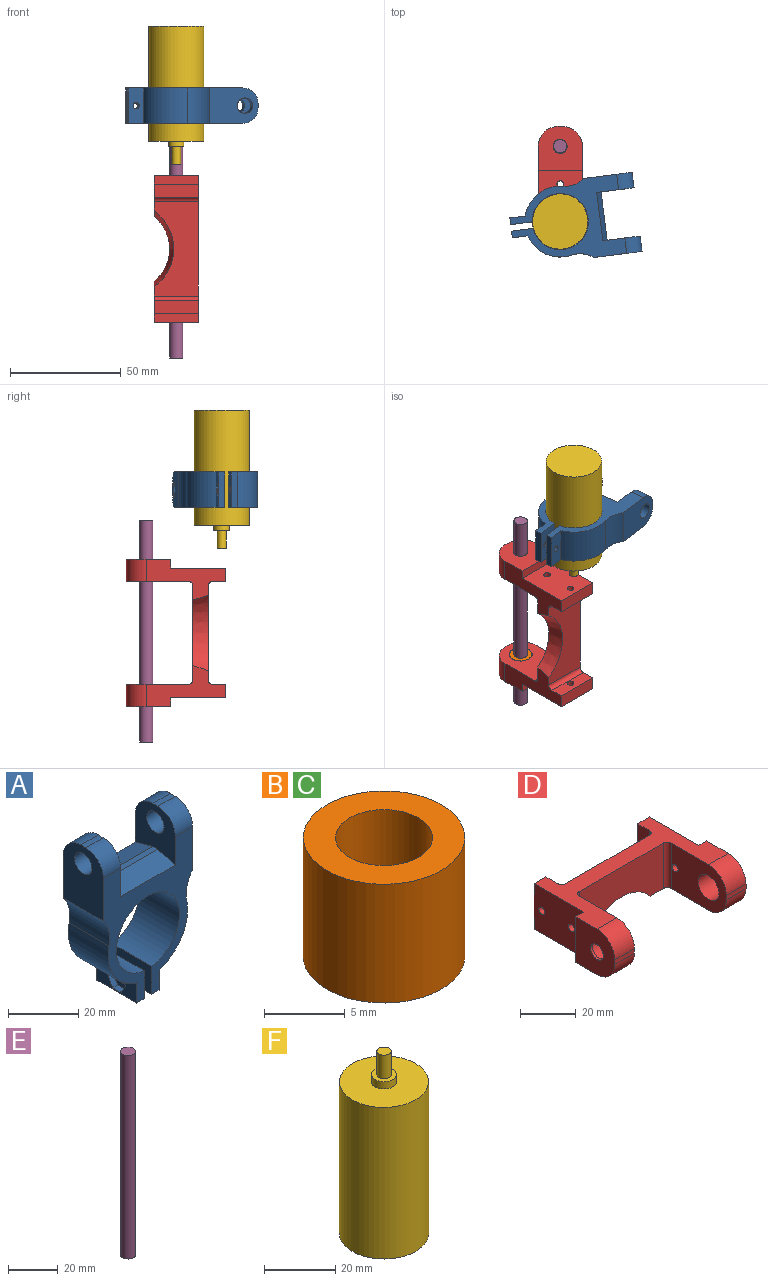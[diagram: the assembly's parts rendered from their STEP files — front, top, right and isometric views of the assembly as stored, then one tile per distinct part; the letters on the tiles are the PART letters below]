
ASSEMBLY  parts=6 mates=4
PART A: 37 faces, bbox 36x16x57.4 mm
  f0: plane 7x2mm, normal (0,0,1), area 14mm2, adj f23,f25,f27,f30
  f1: cylinder r=7mm len=7mm, axis (-1,0,0), area 77mm2, adj f14,f24,f26,f31
  f2: cylinder r=7mm len=7mm, axis (-1,0,0), area 77mm2, adj f13,f24,f26,f31
  f3: cylinder r=16mm len=18.55mm, axis (0,1,0), area 380.6mm2, adj f9,f13,f14,f28
  f4: cylinder r=1.4mm len=2.8mm, axis (-1,0,0), area 8.8mm2, adj f11,f16
  f5: plane 16x9.74mm, normal (-1,0,0), area 149.7mm2, adj f6,f12,f13,f14,f15
  f6: plane 16x3mm, normal (0,0,-1), area 48mm2, adj f5,f7,f13,f14
  f7: plane 16x7mm, normal (1,0,0), area 105.8mm2, adj f6,f8,f13,f14,f15
  f8: cylinder r=16mm len=18.55mm, axis (0,1,0), area 380.6mm2, adj f7,f13,f14,f29
  f9: plane 16x7mm, normal (-1,0,0), area 80.8mm2, adj f3,f10,f13,f14,f17,f18,f19,f20
  f10: plane 16x3mm, normal (0,0,-1), area 48mm2, adj f9,f11,f13,f14
  f11: plane 16x9.74mm, normal (1,0,0), area 149.7mm2, adj f4,f10,f12,f13,f14
  f12: cylinder r=12.7mm len=25.4mm, axis (0,1,0), area 1228.6mm2, adj f5,f11,f13,f14
  f13: plane 50.35x36mm, normal (0,-1,0), area 662.2mm2, adj f2,f3,f5,f6,f7,f8,f9,f10
  f14: plane 50.35x36mm, normal (0,1,0), area 662.2mm2, adj f1,f3,f5,f6,f7,f8,f9,f10
  f15: cylinder r=1.4mm len=3mm, axis (-1,0,0), area 26.4mm2, adj f5,f7
  f16: plane 6.93x6mm, normal (-1,0,0), area 25mm2, adj f4,f17,f18,f19,f20,f21,f22
  f17: plane 3x2mm, normal (0,0.87,-0.5), area 6.9mm2, adj f9,f16,f18,f22
  f18: plane 3.46x2mm, normal (0,0,-1), area 6.9mm2, adj f9,f16,f17,f19
  f19: plane 3x2mm, normal (0,-0.87,-0.5), area 6.9mm2, adj f9,f16,f18,f20
  f20: plane 3x2mm, normal (0,-0.87,0.5), area 6.9mm2, adj f9,f16,f19,f21
  f21: plane 3.46x2mm, normal (0,0,1), area 6.9mm2, adj f9,f16,f20,f22
  f22: plane 3x2mm, normal (0,0.87,0.5), area 6.9mm2, adj f9,f16,f17,f21
  f23: cylinder r=7mm len=7mm, axis (-1,0,0), area 77mm2, adj f0,f14,f27,f30
  f24: plane 7x2mm, normal (0,0,1), area 14mm2, adj f1,f2,f26,f31
  f25: cylinder r=7mm len=7mm, axis (-1,0,0), area 77mm2, adj f0,f13,f27,f30
  f26: plane 22x16mm, normal (1,0,0), area 292.5mm2, adj f1,f2,f13,f14,f24,f29,f33
  f27: plane 22x16mm, normal (-1,0,0), area 292.5mm2, adj f0,f13,f14,f23,f25,f28,f34
  f28: cylinder r=12mm len=16mm, axis (0,-1,0), area 166.4mm2, adj f3,f13,f14,f27
  f29: cylinder r=12mm len=16mm, axis (0,1,0), area 166.4mm2, adj f8,f13,f14,f26
  f30: plane 17x16mm, normal (1,0,0), area 194.5mm2, adj f0,f13,f14,f23,f25,f32,f34,f35
  f31: plane 17x16mm, normal (-1,0,0), area 194.5mm2, adj f1,f2,f13,f14,f24,f32,f33,f35
  f32: plane 22x2mm, normal (0,0,1), area 44mm2, adj f30,f31,f35,f36
  f33: cylinder r=3.5mm len=7mm, axis (-1,0,0), area 153.9mm2, adj f26,f31
  f34: cylinder r=3.5mm len=7mm, axis (-1,0,0), area 153.9mm2, adj f27,f30
  f35: plane 22x7mm, normal (0,0.27,0.96), area 160.2mm2, adj f14,f30,f31,f32
  f36: plane 22x7mm, normal (0,-0.27,0.96), area 160.2mm2, adj f13,f30,f31,f32
PART B: 4 faces, bbox 10x10x9 mm
  f0: cylinder r=3mm len=9mm, axis (0,0,-1), area 169.6mm2, adj f2,f3
  f1: cylinder r=5mm len=10mm, axis (0,0,-1), area 282.7mm2, adj f2,f3
  f2: plane 10x10mm, normal (0,0,1), area 50.3mm2, adj f0,f1
  f3: plane 10x10mm, normal (0,0,-1), area 50.3mm2, adj f0,f1
PART C: same geometry as B
PART D: 38 faces, bbox 66.7x45.1x21.2 mm
  f0: plane 42.6x20mm, normal (0,-1,0), area 708.5mm2, adj f1,f8,f9,f21,f22,f31
  f1: plane 36.08x18.65mm, normal (0,0,-1), area 313.4mm2, adj f0,f2,f3,f4,f5,f7,f8,f18
  f2: plane 20x6mm, normal (0,1,0), area 120mm2, adj f1,f3,f20,f21
  f3: plane 25x20mm, normal (-1,0,0), area 485.9mm2, adj f1,f2,f4,f21,f23,f26
  f4: plane 20x4mm, normal (0,1,0), area 80mm2, adj f1,f3,f5,f21
  f5: plane 20x20mm, normal (-1,0,0), area 333.1mm2, adj f1,f4,f6,f21,f32,f35,f37
  f6: plane 10x2mm, normal (0,-1,0), area 20mm2, adj f5,f7,f35,f37
  f7: plane 28x20mm, normal (1,0,0), area 433.2mm2, adj f1,f6,f8,f21,f26,f29,f35,f37
  f8: cylinder r=2mm len=20mm, axis (0,0,-1), area 62.8mm2, adj f0,f1,f7,f21
  f9: cylinder r=2mm len=20mm, axis (0,0,-1), area 62.8mm2, adj f0,f10,f21,f22
  f10: plane 28x20mm, normal (-1,0,0), area 433.2mm2, adj f9,f11,f21,f22,f25,f28,f34,f36
  f11: plane 10x2mm, normal (0,-1,0), area 20mm2, adj f10,f12,f34,f36
  f12: plane 20x20mm, normal (1,0,0), area 333.1mm2, adj f11,f13,f21,f22,f33,f34,f36
  f13: plane 20x4mm, normal (0,1,0), area 80mm2, adj f12,f14,f21,f22
  f14: plane 25x20mm, normal (1,0,0), area 485.9mm2, adj f13,f15,f21,f22,f24,f25
  f15: plane 20x6mm, normal (0,1,0), area 120mm2, adj f14,f16,f21,f22
  f16: plane 20x6mm, normal (-1,0,0), area 112.9mm2, adj f15,f17,f21,f22,f24
  f17: cylinder r=2mm len=20mm, axis (0,0,-1), area 62.8mm2, adj f16,f18,f21,f22
  f18: plane 42.6x20mm, normal (0,1,0), area 639.3mm2, adj f1,f17,f19,f21,f22,f31
  f19: cylinder r=2mm len=20mm, axis (0,0,-1), area 62.8mm2, adj f1,f18,f20,f21
  f20: plane 20x6mm, normal (1,0,0), area 112.9mm2, adj f1,f2,f19,f21,f23
  f21: plane 66.6x36mm, normal (0,0,1), area 849.6mm2, adj f0,f2,f3,f4,f5,f7,f8,f9
  f22: plane 36.08x18.65mm, normal (0,0,-1), area 313.4mm2, adj f0,f9,f10,f12,f13,f14,f15,f16
  f23: cylinder r=1.5mm len=6mm, axis (1,0,0), area 56.5mm2, adj f3,f20
  f24: cylinder r=1.5mm len=6mm, axis (1,0,0), area 56.5mm2, adj f14,f16
  f25: cylinder r=1.5mm len=6mm, axis (1,0,0), area 56.5mm2, adj f10,f14
  f26: cylinder r=1.5mm len=6mm, axis (1,0,0), area 56.5mm2, adj f3,f7
  f27: plane 10.4x10.4mm, normal (-1,0,0), area 52.8mm2, adj f28,f33
  f28: cylinder r=5.2mm len=10.4mm, axis (1,0,0), area 294.1mm2, adj f10,f27
  f29: cylinder r=5.2mm len=10.4mm, axis (1,0,0), area 294.1mm2, adj f7,f30
  f30: plane 10.4x10.4mm, normal (1,0,0), area 52.8mm2, adj f29,f32
  f31: cone r=19mm half-angle=15deg, axis (0,1,0), area 266.8mm2, adj f0,f1,f18,f22
  f32: cylinder r=3.2mm len=6.4mm, axis (-1,0,0), area 20.1mm2, adj f5,f30
  f33: cylinder r=3.2mm len=6.4mm, axis (-1,0,0), area 20.1mm2, adj f12,f27
  f34: cylinder r=9mm len=10mm, axis (1,0,0), area 141.4mm2, adj f10,f11,f12,f22
  f35: cylinder r=9mm len=10mm, axis (1,0,0), area 141.4mm2, adj f1,f5,f6,f7
  f36: cylinder r=9mm len=10mm, axis (-1,0,0), area 141.4mm2, adj f10,f11,f12,f21
  f37: cylinder r=9mm len=10mm, axis (-1,0,0), area 141.4mm2, adj f5,f6,f7,f21
PART E: 3 faces, bbox 6x6x100 mm
  f0: cylinder r=3mm len=100mm, axis (0,0,-1), area 1885mm2, adj f1,f2
  f1: plane 6x6mm, normal (0,0,1), area 28.3mm2, adj f0
  f2: plane 6x6mm, normal (0,0,-1), area 28.3mm2, adj f0
PART F: 7 faces, bbox 25x25x62.5 mm
  f0: cylinder r=12.5mm len=52mm, axis (0,0,-1), area 4084.1mm2, adj f1,f2
  f1: plane 25x25mm, normal (0,0,1), area 452.4mm2, adj f0,f3
  f2: plane 25x25mm, normal (0,0,-1), area 490.9mm2, adj f0
  f3: cylinder r=3.5mm len=7mm, axis (0,0,-1), area 55mm2, adj f1,f4
  f4: plane 7x7mm, normal (0,0,1), area 25.9mm2, adj f3,f5
  f5: cylinder r=2mm len=8mm, axis (0,0,-1), area 100.5mm2, adj f4,f6
  f6: plane 4x4mm, normal (0,0,1), area 12.6mm2, adj f5
PLACE A rot(axis=(-0.63,0.55,-0.55),115.9deg) t=(-20.42,-12.73,63.15)mm
PLACE B t=(-20.42,21.34,-33.86)mm
PLACE C t=(-20.42,21.34,21.74)mm
PLACE D rot(axis=(-0.71,0,-0.71),180deg) t=(-30.42,0.34,-1.56)mm fixed
PLACE E rot(axis=(0.71,0.71,0),180deg) t=(-20.42,21.34,49.14)mm
PLACE F rot(axis=(0.66,0.75,0),180deg) t=(-20.42,-12.73,99.15)mm
MATE fastened B.f1 <-> D.f28  axis (0,0,-1) through (-20.42,21.34,-33.86)mm
MATE fastened D.f28 <-> C.f1  axis (0,0,-1) through (-20.42,21.34,30.74)mm
MATE slider F.f0 <-> A.f12  axis (0,0,1) through (-20.42,-12.73,73.15)mm
MATE revolute E.f0 <-> B.f0  axis (0,0,1) through (-20.42,21.34,-0.86)mm
